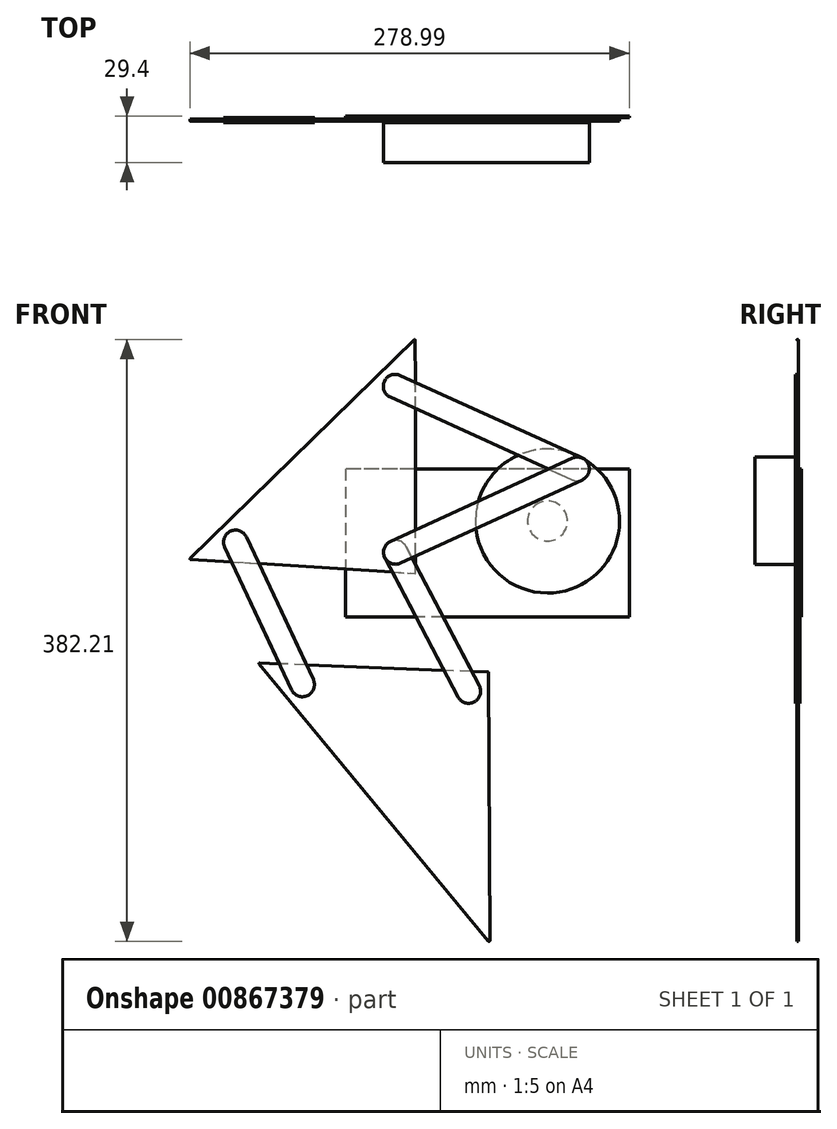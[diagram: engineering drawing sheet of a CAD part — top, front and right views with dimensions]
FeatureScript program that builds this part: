
annotation { "Feature Type Name" : "Feature", "Feature Type Description" : "" }
export const myFeature = defineFeature(function(context is Context, id is Id, definition is map)
    precondition{}
    {
        {
            assignVariable(context, id + "F0", {"name" : "Scale", "anyValue" : .1});
        }
        {
            assignVariable(context, id + "F1", {"name" : "thickness", "anyValue" : 1});
        }
        {
            var Q0;
            Q0=qCreatedBy(makeId("Front.planeOp"),FACE);
            var sketch = newSketch(context, id + "F2", { "sketchPlane" : qUnion([Q0])});
            skLineSegment(sketch, "E0", {"start": v(-155.7, -103.98) * mm, "end": v(-50.11, -108.2) * mm});
            skLineSegment(sketch, "E1", {"start": v(-50.11, -108.2) * mm, "end": v(-49.42, -232.65) * mm});
            skLineSegment(sketch, "E2", {"start": v(-49.42, -232.65) * mm, "end": v(-155.7, -103.98) * mm});
            skLineSegment(sketch, "E3", {"start": v(-50.11, -108.2) * mm, "end": v(-96.52, -19.81) * mm});
            skLineSegment(sketch, "E4", {"start": v(-96.52, -19.81) * mm, "end": v(-198.17, -13.37) * mm});
            skLineSegment(sketch, "E5", {"start": v(-198.17, -13.37) * mm, "end": v(-155.7, -103.98) * mm});
            skLineSegment(sketch, "E6", {"start": v(-50.11, -108.2) * mm, "end": v(18.91, 33.07) * mm});
            skLineSegment(sketch, "E7", {"start": v(18.91, 33.07) * mm, "end": v(-96.71, 85.6) * mm});
            skLineSegment(sketch, "E8", {"start": v(-96.71, 85.6) * mm, "end": v(-96.52, -19.81) * mm});
            skLineSegment(sketch, "E9", {"start": v(-96.71, 85.6) * mm, "end": v(-198.17, -13.37) * mm});
            skCircle(sketch, "E10", {"center": v(0, 0) * mm, "radius": 38.1 * mm, "construction": true});
            skLineSegment(sketch, "E11", {"start": v(0, 0) * mm, "end": v(0, -19.81) * mm, "construction": true});
            skLineSegment(sketch, "E12", {"start": v(0, -19.81) * mm, "end": v(-96.52, -19.81) * mm, "construction": true});
            skPoint(sketch, "E13", {"position": v(18.91, 33.07) * mm});
            skSolve(sketch);
        }
        {
            var Q0;
            Q0=makeQuery(id+"F2.imprint","IMPRINT",FACE,{"disambiguationData":[TD([[makeQuery(id+"F2.imprint","IMPRINT",EDGE,{"derivedFrom":sQuery(id+"F2.wireOp",EDGE,"E0")}),-1.0]])]});
            var sketch = newSketch(context, id + "F3", { "sketchPlane" : qUnion([Q0])});
            skLineSegment(sketch, "E14.0", {"start": v(-83.8, -33.34) * mm, "end": v(-84.07, 115.67) * mm});
            skLineSegment(sketch, "E14.1", {"start": v(-227.5, -24.24) * mm, "end": v(-83.8, -33.34) * mm});
            skLineSegment(sketch, "E14.2", {"start": v(-84.07, 115.67) * mm, "end": v(-227.5, -24.24) * mm});
            skLineSegment(sketch, "E15.0", {"start": v(-183.58, -90.16) * mm, "end": v(-36.52, -268.2) * mm});
            skLineSegment(sketch, "E15.1", {"start": v(-37.48, -95.98) * mm, "end": v(-183.58, -90.16) * mm});
            skLineSegment(sketch, "E15.2", {"start": v(-36.52, -268.2) * mm, "end": v(-37.48, -95.98) * mm});
            skPoint(sketch, "E16.0", {"position": v(-96.71, 85.6) * mm});
            skPoint(sketch, "E17.0", {"position": v(-96.52, -19.81) * mm});
            skPoint(sketch, "E18.0", {"position": v(-198.17, -13.37) * mm});
            skPoint(sketch, "E19.0", {"position": v(-155.7, -103.98) * mm});
            skPoint(sketch, "E20.0", {"position": v(-50.11, -108.2) * mm});
            skPoint(sketch, "E21.0", {"position": v(-49.42, -232.65) * mm});
            skCircle(sketch, "E22.0", {"center": v(0, 0) * mm, "radius": 38.1 * mm, "construction": true});
            skPoint(sketch, "E22.1", {"position": v(0, 0) * mm});
            skPoint(sketch, "E22.2", {"position": v(18.91, 33.07) * mm});
            skCircle(sketch, "E23.0", {"center": v(0, 0) * mm, "radius": 45.72 * mm});
            skSolve(sketch);
        }
        {
            var Q0;
            Q0 = qSketchRegion(id + "F3", true);
            extrude(context, id + "F4", {"entities" : qUnion([Q0]), "depth" : (getVariable(context, 'thickness')) * mm, "offsetDistance" : 25.4 * mm});
        }
        {
            var Q0;
            Q0=makeQuery(id+"F4.opExtrude","SWEPT_EDGE",EDGE,{"disambiguationData":[OSD([sQuery(id+"F3.wireOp",EDGE,"E14.0"),sQuery(id+"F3.wireOp",EDGE,"E14.1")])]});
            var Q1;
            Q1=makeQuery(id+"F4.opExtrude","SWEPT_EDGE",EDGE,{"disambiguationData":[OSD([sQuery(id+"F3.wireOp",EDGE,"E14.1"),sQuery(id+"F3.wireOp",EDGE,"E14.2")])]});
            var Q2;
            Q2=makeQuery(id+"F4.opExtrude","SWEPT_EDGE",EDGE,{"disambiguationData":[OSD([sQuery(id+"F3.wireOp",EDGE,"E15.0"),sQuery(id+"F3.wireOp",EDGE,"E15.1")])]});
            var Q3;
            Q3=makeQuery(id+"F4.opExtrude","SWEPT_EDGE",EDGE,{"disambiguationData":[OSD([sQuery(id+"F3.wireOp",EDGE,"E15.1"),sQuery(id+"F3.wireOp",EDGE,"E15.2")])]});
            var Q4;
            Q4=makeQuery(id+"F4.opExtrude","SWEPT_EDGE",EDGE,{"disambiguationData":[OSD([sQuery(id+"F3.wireOp",EDGE,"E14.0"),sQuery(id+"F3.wireOp",EDGE,"E14.2")])]});
            fillet(context, id + "F5", {"entities" : qUnion([Q0, Q1, Q2, Q3, Q4]), "radius" : (getVariable(context, 'Scale') * 3) * mm, "tangentPropagation" : true, "allowEdgeOverflow" : false});
        }
        {
            var Q0;
            Q0=makeQuery(id+"F4.opExtrude","SWEPT_EDGE",EDGE,{"disambiguationData":[OSD([sQuery(id+"F3.wireOp",EDGE,"E15.0"),sQuery(id+"F3.wireOp",EDGE,"E15.2")])]});
            fillet(context, id + "F6", {"entities" : qUnion([Q0]), "radius" : (getVariable(context, 'Scale') * 7) * mm, "tangentPropagation" : true, "allowEdgeOverflow" : false});
        }
        {
            var Q0;
            Q0=qCreatedBy(makeId("Front.planeOp"),FACE);
            var sketch = newSketch(context, id + "F7", { "sketchPlane" : qUnion([Q0])});
            skPoint(sketch, "E24.0", {"position": v(-198.17, -13.37) * mm});
            skPoint(sketch, "E25.0", {"position": v(-96.52, -19.81) * mm});
            skPoint(sketch, "E26.0", {"position": v(-50.11, -108.2) * mm});
            skPoint(sketch, "E27.0", {"position": v(-155.7, -103.98) * mm});
            skLineSegment(sketch, "E28", {"start": v(-50.11, -108.2) * mm, "end": v(-96.52, -19.81) * mm, "construction": true});
            skLineSegment(sketch, "E29", {"start": v(-155.7, -103.98) * mm, "end": v(-198.17, -13.37) * mm, "construction": true});
            skLineSegment(sketch, "E30.0", {"start": v(-162.6, -107.22) * mm, "end": v(-205.07, -16.6) * mm});
            skLineSegment(sketch, "E31.MirrorCS", {"start": v(-148.8, -100.75) * mm, "end": v(-191.27, -10.14) * mm});
            skArc(sketch, "E32", {"start": v(-191.27, -10.14) * mm, "mid": v(-201.4, -6.47) * mm, "end": v(-205.07, -16.6) * mm});
            skArc(sketch, "E33", {"start": v(-162.6, -107.22) * mm, "mid": v(-152.46, -110.88) * mm, "end": v(-148.8, -100.75) * mm});
            skLineSegment(sketch, "E34.0", {"start": v(-56.86, -111.73) * mm, "end": v(-103.27, -23.35) * mm});
            skLineSegment(sketch, "E35.MirrorCS", {"start": v(-43.37, -104.65) * mm, "end": v(-89.77, -16.27) * mm});
            skArc(sketch, "E36", {"start": v(-103.27, -23.35) * mm, "mid": v(-100.06, -13.07) * mm, "end": v(-89.77, -16.27) * mm});
            skArc(sketch, "E37", {"start": v(-43.37, -104.65) * mm, "mid": v(-46.57, -114.94) * mm, "end": v(-56.86, -111.73) * mm});
            skCircle(sketch, "E38", {"center": v(0, 0) * mm, "radius": 12.7 * mm});
            skSolve(sketch);
        }
        {
            var Q0;
            Q0 = qSketchRegion(id + "F7", true);
            extrude(context, id + "F8", {"entities" : qUnion([Q0]), "oppositeDirection" : true, "depth" : (getVariable(context, 'thickness')) * mm, "offsetDistance" : 25.4 * mm});
        }
        {
            var Q0;
            Q0=makeQuery(id+"F4.opExtrude","CAP_FACE",FACE,{"disambiguationData":[OSD([sQuery(id+"F3.wireOp",EDGE,"E15.0"),sQuery(id+"F3.wireOp",EDGE,"E15.1"),sQuery(id+"F3.wireOp",EDGE,"E15.2")])],"isStart":false});
            var sketch = newSketch(context, id + "F9", { "sketchPlane" : qUnion([Q0])});
            skPoint(sketch, "E39.0", {"position": v(-198.17, -13.37) * mm});
            skPoint(sketch, "E39.1", {"position": v(-96.52, -19.81) * mm});
            skPoint(sketch, "E39.2", {"position": v(-50.11, -108.2) * mm});
            skPoint(sketch, "E39.3", {"position": v(-155.7, -103.98) * mm});
            skLineSegment(sketch, "E39.6", {"start": v(-162.6, -107.22) * mm, "end": v(-205.07, -16.6) * mm});
            skLineSegment(sketch, "E39.7", {"start": v(-148.8, -100.75) * mm, "end": v(-191.27, -10.14) * mm});
            skArc(sketch, "E39.8", {"start": v(-191.27, -10.14) * mm, "mid": v(-201.4, -6.47) * mm, "end": v(-205.07, -16.6) * mm});
            skArc(sketch, "E39.9", {"start": v(-162.6, -107.22) * mm, "mid": v(-152.46, -110.88) * mm, "end": v(-148.8, -100.75) * mm});
            skLineSegment(sketch, "E39.10", {"start": v(-56.86, -111.73) * mm, "end": v(-103.27, -23.35) * mm});
            skLineSegment(sketch, "E39.11", {"start": v(-43.37, -104.65) * mm, "end": v(-89.77, -16.27) * mm});
            skArc(sketch, "E39.12", {"start": v(-103.27, -23.35) * mm, "mid": v(-100.06, -13.07) * mm, "end": v(-89.77, -16.27) * mm});
            skArc(sketch, "E39.13", {"start": v(-43.37, -104.65) * mm, "mid": v(-46.57, -114.94) * mm, "end": v(-56.86, -111.73) * mm});
            skPoint(sketch, "E40.0", {"position": v(-96.71, 85.6) * mm});
            skCircle(sketch, "E41.0", {"center": v(0, 0) * mm, "radius": 38.1 * mm, "construction": true});
            skPoint(sketch, "E41.1", {"position": v(18.91, 33.07) * mm});
            skPoint(sketch, "E41.2", {"position": v(0, 0) * mm});
            skLineSegment(sketch, "E42", {"start": v(-96.71, 85.6) * mm, "end": v(18.91, 33.07) * mm, "construction": true});
            skLineSegment(sketch, "E43.0", {"start": v(-99.87, 78.66) * mm, "end": v(15.76, 26.14) * mm});
            skLineSegment(sketch, "E44.MirrorCS", {"start": v(-93.56, 92.54) * mm, "end": v(22.07, 40.01) * mm});
            skArc(sketch, "E45", {"start": v(-93.56, 92.54) * mm, "mid": v(-103.65, 88.75) * mm, "end": v(-99.87, 78.66) * mm});
            skArc(sketch, "E46", {"start": v(15.76, 26.14) * mm, "mid": v(25.85, 29.92) * mm, "end": v(22.07, 40.01) * mm});
            skSolve(sketch);
        }
        {
            var Q0;
            Q0 = qSketchRegion(id + "F9", true);
            extrude(context, id + "F10", {"entities" : qUnion([Q0]), "depth" : (getVariable(context, 'thickness')) * mm, "offsetDistance" : 25.4 * mm});
        }
        {
            var Q0;
            Q0=makeQuery(id+"F10.opExtrude","CAP_FACE",FACE,{"disambiguationData":[OSD([sQuery(id+"F9.wireOp",EDGE,"E39.10"),sQuery(id+"F9.wireOp",EDGE,"E39.11"),sQuery(id+"F9.wireOp",EDGE,"E39.12"),sQuery(id+"F9.wireOp",EDGE,"E39.13")])],"isStart":false});
            var sketch = newSketch(context, id + "F11", { "sketchPlane" : qUnion([Q0])});
            skCircle(sketch, "E47.0", {"center": v(0, 0) * mm, "radius": 38.1 * mm, "construction": true});
            skPoint(sketch, "E47.1", {"position": v(18.91, 33.07) * mm});
            skPoint(sketch, "E47.2", {"position": v(0, 0) * mm});
            skPoint(sketch, "E47.3", {"position": v(-96.52, -19.81) * mm});
            skLineSegment(sketch, "E48", {"start": v(-96.52, -19.81) * mm, "end": v(18.91, 33.07) * mm, "construction": true});
            skLineSegment(sketch, "E49.0", {"start": v(-93.35, -26.74) * mm, "end": v(22.09, 26.15) * mm});
            skLineSegment(sketch, "E50.MirrorCS", {"start": v(-99.7, -12.88) * mm, "end": v(15.74, 40) * mm});
            skArc(sketch, "E51", {"start": v(22.09, 26.15) * mm, "mid": v(25.84, 36.25) * mm, "end": v(15.74, 40) * mm});
            skArc(sketch, "E52", {"start": v(-99.7, -12.88) * mm, "mid": v(-103.45, -22.99) * mm, "end": v(-93.35, -26.74) * mm});
            skSolve(sketch);
        }
        {
            var Q0;
            Q0 = qSketchRegion(id + "F11", true);
            extrude(context, id + "F12", {"entities" : qUnion([Q0]), "depth" : 25.4 * mm, "offsetDistance" : 25.4 * mm});
        }
        {
            var Q0;
            Q0=makeQuery(id+"F8.opExtrude","CAP_FACE",FACE,{"disambiguationData":[OSD([sQuery(id+"F7.wireOp",EDGE,"E38")])],"isStart":false});
            var sketch = newSketch(context, id + "F13", { "sketchPlane" : qUnion([Q0])});
            skLineSegment(sketch, "E53.bottom", {"start": v(-51.88, 33.17) * mm, "end": v(128.35, 33.17) * mm});
            skLineSegment(sketch, "E53.top", {"start": v(-51.88, -60.93) * mm, "end": v(128.35, -60.93) * mm});
            skLineSegment(sketch, "E53.left", {"start": v(-51.88, 33.17) * mm, "end": v(-51.88, -60.93) * mm});
            skLineSegment(sketch, "E53.right", {"start": v(128.35, 33.17) * mm, "end": v(128.35, -60.93) * mm});
            skSolve(sketch);
        }
        {
            var Q0;
            Q0=makeQuery(id+"F13.imprint","IMPRINT",FACE,{"disambiguationData":[TD([[makeQuery(id+"F13.imprint","IMPRINT",EDGE,{"derivedFrom":sQuery(id+"F13.wireOp",EDGE,"E53.bottom")}),-1.0]])]});
            var Q1;
            Q1=makeQuery(id+"F13.imprint","IMPRINT",FACE,{"disambiguationData":[TD([[makeQuery(id+"F13.imprint","IMPRINT",EDGE,{"derivedFrom":makeQuery(id+"F8.opExtrude","CAP_EDGE",EDGE,{"disambiguationData":[OSD([sQuery(id+"F7.wireOp",EDGE,"E38")])],"isStart":false})}),-1.0]])]});
            extrude(context, id + "F14", {"entities" : qUnion([Q0, Q1]), "depth" : (getVariable(context, 'thickness')) * mm, "offsetDistance" : 25.4 * mm});
        }
    });
